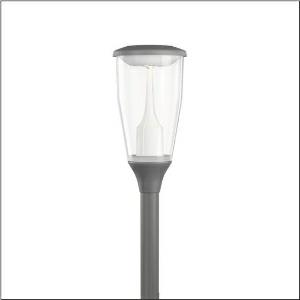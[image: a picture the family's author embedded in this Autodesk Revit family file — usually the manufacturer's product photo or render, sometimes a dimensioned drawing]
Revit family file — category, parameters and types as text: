
# Revit family: dl_11_iq___st1_2a_5xa5565ef14h000022_473d
name_source: partatom
category: Lighting Fixtures
units: mm (PartAtom-declared; Revit-internal decimal feet)

## family parameters
Cut with Voids When Loaded = No
Host = Face
Light Source = No
Part Type = Normal
Room Calculation Point = No
Round Connector Dimension = Use Diameter
Shared = No

## types (1)
- --- (1 x LED, 1560 lm, 10.5 W, 3000K)
    Apparent Load = 11 VA
    CIE Flux Codes = 24 63 94 96 100
    Color Rendering = 70
    Color Temperature = 3000K
    Default Elevation = 1800 mm
    Description = DL 11 iQ, mast luminaire, Module 540 iQ-SR, primary light control with 3 zone facetted reflector, of plastic, silver coated, highly specular, structured, primary optical cover: cover, of PMMA, transparent, light distribution: ST1.2a, light emission: direct distribution, primary light characteristic: asymmetric, installation type: post-top, LED, High Power LED, rated luminous flux: 1.560lm, luminous efficacy: 149lm/W, light colour: 730, colour temperature: 3000K, control gear: iQ Street-Remote, control: Street-Remote, Auto-Match, Temp-Guard, Lumen-Switch, Night-Set, Smart-Wire, Light-Fading, Desk-Remote (wireless, voltage-free reading and setting of iQ features in the workshop via application-optimized NFC function/RFID function), optimised constant luminous flux control (CLO 2.0), mains connection: 220..240V, AC, 50/60Hz, connection cable pre-assembled, cable length: 5,5m, start of lifetime: 11W, end of service life: 11W, reduction: 5W, luminaire housing, upper part, of diecast aluminium, coated, Siteco® metallic grey (DB 702S), spigot size: 60mm (post-top), mounting height: 3..5m, post-top mast mounting element, of diecast aluminium, coated, Siteco® metallic grey (DB 702S), Module 540 iQ-SR, traffic white (RAL 9016), equipment: standard, protection rating (complete): IP66, insulation class (complete): insulation class II (safety insulation), certification: CE, ENEC, ENEC+, VDE, impact resistance: IK07, packaging unit: 1 piece

Light Distribution: ST1.2a
    Height = 665 mm
    Lamp = 1 x LED
    Lamp Light Flux = 1560 lm
    Lamp Power = 10.5 W
    Lamp count = 1
    Length = 334 mm
    Luminous efficacy = 149 lm/W
    Manufacturer = Siteco
    ModVariant = No
    Model = 5XA5565EF14H000022
    Number of Poles = 1
    OnlyDefault = Yes
    Power Factor = 1
    Product Name = DL 11 iQ | ST1.2a
    Product group = mast luminaire | pylon top
    ProductGroupID = 6100
    Protection Class = Protection class II
    Protection Degree = IP 66
    RLX_Detail_Level = 1
    RLX_Emergency_Light_Flux = 0 lm
    RLX_Emergency_Type = 0
    RLX_Emergency_Type_DB = No
    RlxData = <blob elided: 139969 chars, md5=6ce13ec2>
    Socket = socket
    Standby Power = 0 W
    System Light Flux = 1560 lm
    System Power = 11 W
    Type Comments = factory setting: luminous flux: 100 % | dim-lin: 254 | 419 mA
    Type Image = l_1258354.jpg
    URL = http://relux.com
    VarID = @adj_116763
    Voltage = 0 V
    Weight = 0.00 kg
    Width = 0 mm  [stored 0 ft]

note: [stored X ft] marks values corroborated as IEEE doubles in the binary element streams (Revit-internal decimal feet)

## geometry (parser evidence)
native form markers: Blend x4, Sweep x9
no freeform markers — native parametric forms only
